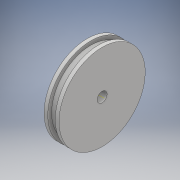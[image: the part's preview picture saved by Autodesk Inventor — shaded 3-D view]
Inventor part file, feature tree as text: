
AUTODESK INVENTOR PART (.ipt)
format: ipt  version: 2018 (Build 220112000, 112)  size: 120,320 bytes
history: native  units: mm
features: sketch x2, revolve x1, extrude x1, other x1
ambient origin geometry x8: Origin, YZ Plane, XZ Plane, XY Plane, X Axis, Y Axis, Z Axis, Center Point
bodies: Body1 (feature_tree)
feature tree (5):
  revolve  "Revolution1"  [1 undecoded]
  extrude  "Extrusion3"  Depth=3.0mm
  other  "Work Axis1"
  sketch  "Sketch4"  dims[d11=6.0mm d12=15.75mm]
  sketch  "Sketch5"  dims[d13=1.5mm d14=3.0mm d15=90.0deg d16=4.0mm d17=8.0mm d18=0.0mm]
note: 1 required parameter value undecoded (feature->parameter linkage not recoverable at this tier; creation-order binding heuristic only, values carry confidence <= 0.55)
